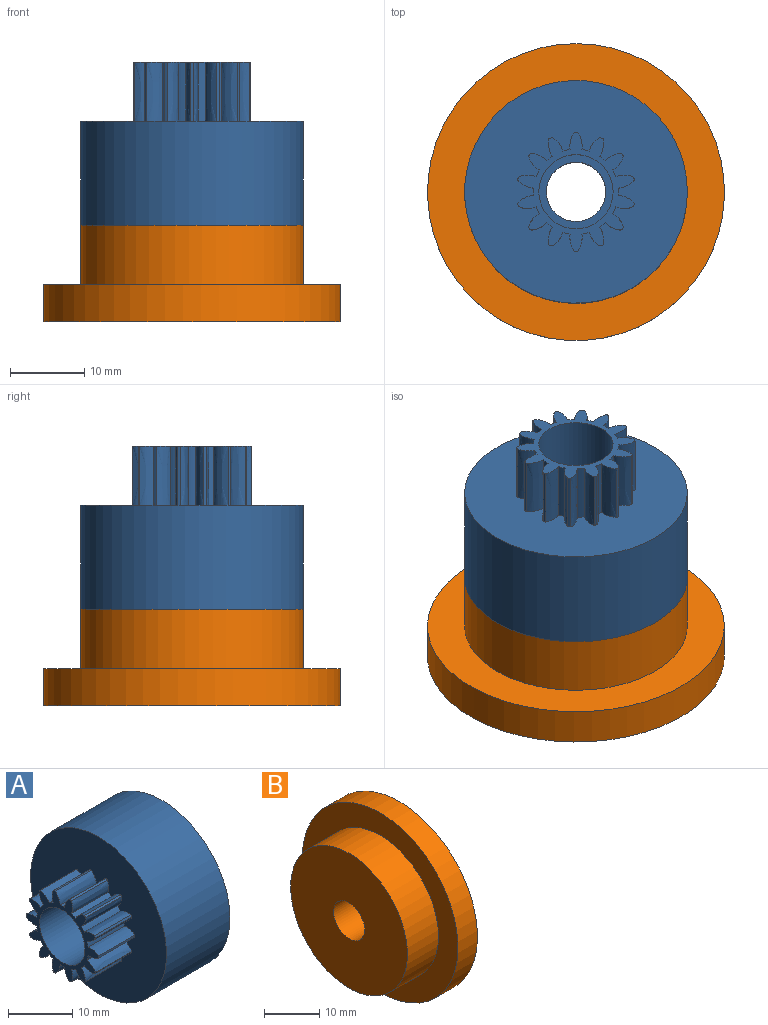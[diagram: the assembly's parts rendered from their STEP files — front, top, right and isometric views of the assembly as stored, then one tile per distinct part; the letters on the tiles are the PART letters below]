
ASSEMBLY  parts=2 mates=1
PART A: 65 faces, bbox 22x30x30 mm
  f0: plane 16x15.68mm, normal (-1,0,0), area 67.7mm2, adj f1,f2,f3,f4,f5,f6,f7,f8
  f1: cylinder r=8mm len=8mm, axis (-1,0,0), area 3.1mm2, adj f0,f16,f19,f59
  f2: cylinder r=8mm len=8mm, axis (-1,0,0), area 3.1mm2, adj f0,f16,f56,f58
  f3: cylinder r=8mm len=8mm, axis (-1,0,0), area 3.1mm2, adj f0,f16,f53,f55
  f4: cylinder r=8mm len=8mm, axis (-1,0,0), area 3.1mm2, adj f0,f16,f50,f52
  f5: cylinder r=8mm len=8mm, axis (-1,0,0), area 3.1mm2, adj f0,f16,f47,f49
  f6: cylinder r=8mm len=8mm, axis (-1,0,0), area 3.1mm2, adj f0,f16,f44,f46
  f7: cylinder r=8mm len=8mm, axis (-1,0,0), area 3.1mm2, adj f0,f16,f41,f43
  f8: cylinder r=8mm len=8mm, axis (-1,0,0), area 3.1mm2, adj f0,f16,f38,f40
  f9: cylinder r=8mm len=8mm, axis (-1,0,0), area 3.1mm2, adj f0,f16,f35,f37
  f10: cylinder r=8mm len=8mm, axis (-1,0,0), area 3.1mm2, adj f0,f16,f32,f34
  f11: cylinder r=8mm len=8mm, axis (-1,0,0), area 3.1mm2, adj f0,f16,f29,f31
  f12: cylinder r=8mm len=8mm, axis (-1,0,0), area 3.1mm2, adj f0,f16,f26,f28
  f13: cylinder r=8mm len=8mm, axis (-1,0,0), area 3.1mm2, adj f0,f16,f23,f25
  f14: plane 30x30mm, normal (1,0,0), area 175.9mm2, adj f15,f64
  f15: cylinder r=15mm len=30mm, axis (-1,0,0), area 1319.5mm2, adj f14,f16
  f16: plane 30x30mm, normal (-1,0,0), area 560.6mm2, adj f1,f2,f3,f4,f5,f6,f7,f8
  f17: cylinder r=8mm len=8mm, axis (-1,0,0), area 3.1mm2, adj f0,f16,f20,f22
  f18: cylinder r=5.75mm len=8mm, axis (-1,0,0), area 8mm2, adj f0,f16,f19,f20
  f19: extruded ~8x2.11mm, area 19.6mm2, adj f0,f1,f16,f18
  f20: extruded ~8x2.11mm, area 19.6mm2, adj f0,f16,f17,f18
  f21: cylinder r=5.75mm len=8mm, axis (-1,0,0), area 8mm2, adj f0,f16,f22,f23
  f22: extruded ~8x2.38mm, area 19.6mm2, adj f0,f16,f17,f21
  f23: extruded ~8x1.9mm, area 19.6mm2, adj f0,f13,f16,f21
  f24: cylinder r=5.75mm len=8mm, axis (-1,0,0), area 8mm2, adj f0,f16,f25,f26
  f25: extruded ~8x2.17mm, area 19.6mm2, adj f0,f13,f16,f24
  f26: extruded ~8x2.33mm, area 19.6mm2, adj f0,f12,f16,f24
  f27: cylinder r=5.75mm len=8mm, axis (-1,0,0), area 8mm2, adj f0,f16,f28,f29
  f28: extruded ~8x1.82mm, area 19.6mm2, adj f0,f12,f16,f27
  f29: extruded ~8x2.3mm, area 19.6mm2, adj f0,f11,f16,f27
  f30: cylinder r=5.75mm len=8mm, axis (-1,0,0), area 8mm2, adj f0,f16,f31,f32
  f31: extruded ~8x2.3mm, area 19.6mm2, adj f0,f11,f16,f30
  f32: extruded ~8x1.82mm, area 19.6mm2, adj f0,f10,f16,f30
  f33: cylinder r=5.75mm len=8mm, axis (-1,0,0), area 8mm2, adj f0,f16,f34,f35
  f34: extruded ~8x2.33mm, area 19.6mm2, adj f0,f10,f16,f33
  f35: extruded ~8x2.17mm, area 19.6mm2, adj f0,f9,f16,f33
  f36: cylinder r=5.75mm len=8mm, axis (-1,0,0), area 8mm2, adj f0,f16,f37,f38
  f37: extruded ~8x1.9mm, area 19.6mm2, adj f0,f9,f16,f36
  f38: extruded ~8x2.38mm, area 19.6mm2, adj f0,f8,f16,f36
  f39: cylinder r=5.75mm len=8mm, axis (-1,0,0), area 8mm2, adj f0,f16,f40,f41
  f40: extruded ~8x2.11mm, area 19.6mm2, adj f0,f8,f16,f39
  f41: extruded ~8x2.11mm, area 19.6mm2, adj f0,f7,f16,f39
  f42: cylinder r=5.75mm len=8mm, axis (-1,0,0), area 8mm2, adj f0,f16,f43,f44
  f43: extruded ~8x2.38mm, area 19.6mm2, adj f0,f7,f16,f42
  f44: extruded ~8x1.9mm, area 19.6mm2, adj f0,f6,f16,f42
  f45: cylinder r=5.75mm len=8mm, axis (-1,0,0), area 8mm2, adj f0,f16,f46,f47
  f46: extruded ~8x2.17mm, area 19.6mm2, adj f0,f6,f16,f45
  f47: extruded ~8x2.33mm, area 19.6mm2, adj f0,f5,f16,f45
  f48: cylinder r=5.75mm len=8mm, axis (-1,0,0), area 8mm2, adj f0,f16,f49,f50
  f49: extruded ~8x1.82mm, area 19.6mm2, adj f0,f5,f16,f48
  f50: extruded ~8x2.3mm, area 19.6mm2, adj f0,f4,f16,f48
  f51: cylinder r=5.75mm len=8mm, axis (-1,0,0), area 8mm2, adj f0,f16,f52,f53
  f52: extruded ~8x2.3mm, area 19.6mm2, adj f0,f4,f16,f51
  f53: extruded ~8x1.82mm, area 19.6mm2, adj f0,f3,f16,f51
  f54: cylinder r=5.75mm len=8mm, axis (-1,0,0), area 8mm2, adj f0,f16,f55,f56
  f55: extruded ~8x2.33mm, area 19.6mm2, adj f0,f3,f16,f54
  f56: extruded ~8x2.17mm, area 19.6mm2, adj f0,f2,f16,f54
  f57: cylinder r=5.75mm len=8mm, axis (-1,0,0), area 8mm2, adj f0,f16,f58,f59
  f58: extruded ~8x1.9mm, area 19.6mm2, adj f0,f2,f16,f57
  f59: extruded ~8x2.38mm, area 19.6mm2, adj f0,f1,f16,f57
  f60: plane 26x26mm, normal (1,0,0), area 480.7mm2, adj f61,f64
  f61: cylinder r=4mm len=8mm, axis (-1,0,0), area 25.1mm2, adj f60,f62
  f62: plane 10x10mm, normal (-1,0,0), area 28.3mm2, adj f61,f63
  f63: cylinder r=5mm len=10mm, axis (-1,0,0), area 314.2mm2, adj f0,f62
  f64: cylinder r=13mm len=26mm, axis (-1,0,0), area 898.5mm2, adj f14,f60
PART B: 6 faces, bbox 13x40x40 mm
  f0: cylinder r=15mm len=30mm, axis (-1,0,0), area 754mm2, adj f1,f4
  f1: plane 30x30mm, normal (-1,0,0), area 656.6mm2, adj f0,f5
  f2: cylinder r=20mm len=40mm, axis (-1,0,0), area 628.3mm2, adj f3,f4
  f3: plane 40x40mm, normal (1,0,0), area 1206.4mm2, adj f2,f5
  f4: plane 40x40mm, normal (-1,0,0), area 549.8mm2, adj f0,f2
  f5: cylinder r=4mm len=13mm, axis (1,0,0), area 326.7mm2, adj f1,f3
PLACE A rot(axis=(0,1,0),90deg) t=(0,0,-22)mm
PLACE B rot(axis=(0,1,0),90deg) t=(0,0,-22)mm
MATE fastened B.f0 <-> A.f1  axis (0,0,1) through (0,0,-22)mm
